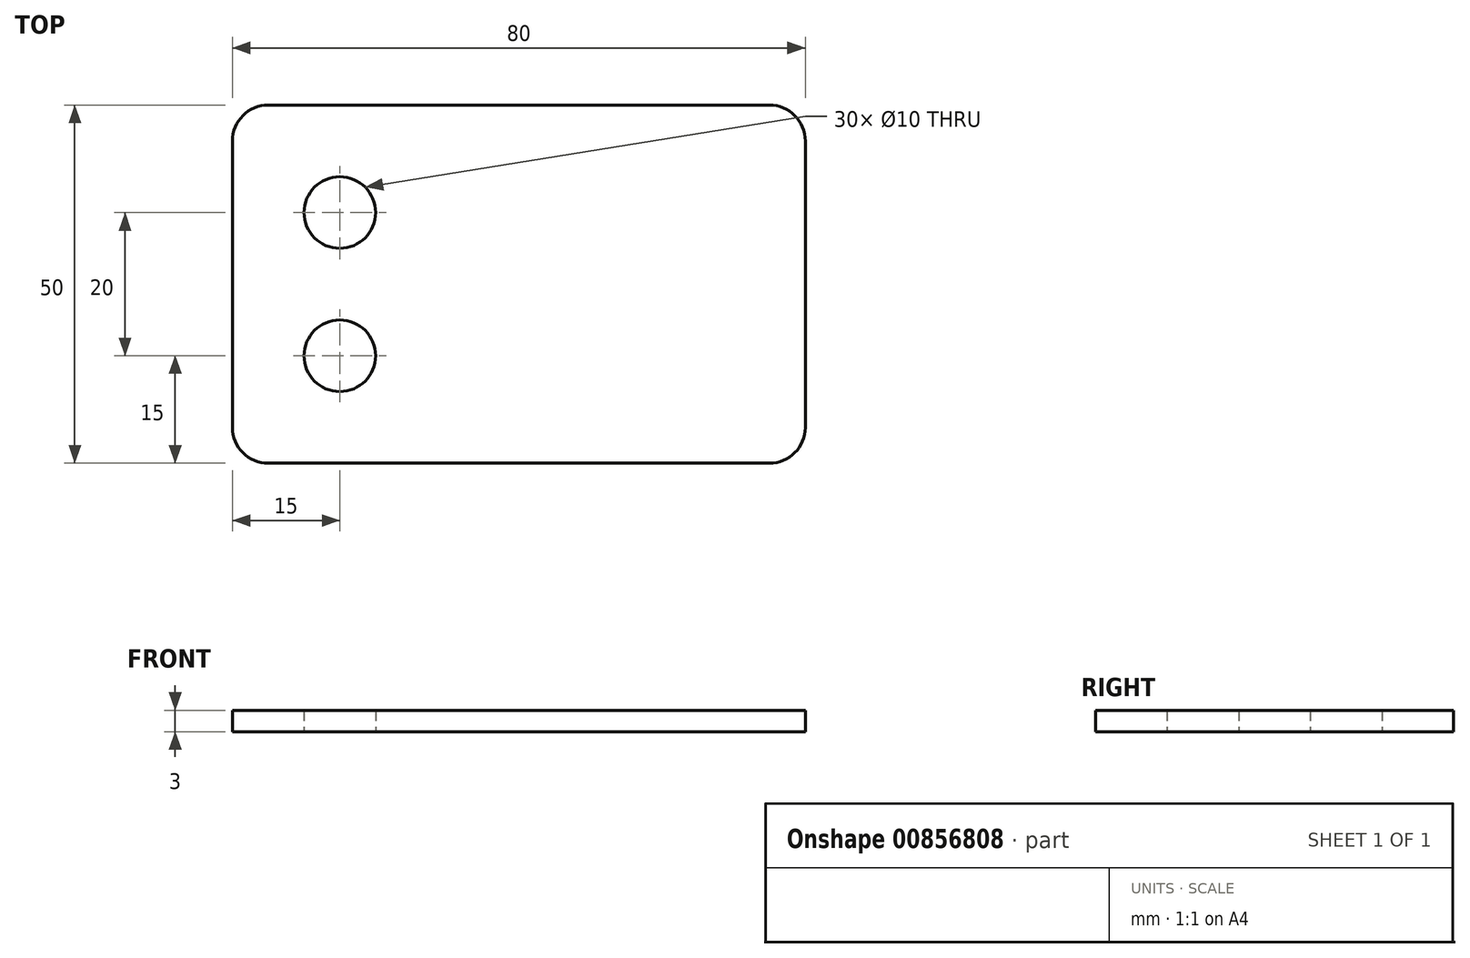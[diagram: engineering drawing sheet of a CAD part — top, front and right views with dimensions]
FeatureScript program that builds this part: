
annotation { "Feature Type Name" : "Feature", "Feature Type Description" : "" }
export const myFeature = defineFeature(function(context is Context, id is Id, definition is map)
    precondition{}
    {
        {
            var Q0;
            Q0=qCreatedBy(makeId("Top.planeOp"),FACE);
            var sketch = newSketch(context, id + "F0", { "sketchPlane" : qUnion([Q0])});
            skLineSegment(sketch, "E0.bottom", {"start": v(40, 25) * mm, "end": v(-40, 25) * mm});
            skLineSegment(sketch, "E0.top", {"start": v(40, -25) * mm, "end": v(-40, -25) * mm});
            skLineSegment(sketch, "E0.left", {"start": v(40, 25) * mm, "end": v(40, -25) * mm});
            skLineSegment(sketch, "E0.right", {"start": v(-40, 25) * mm, "end": v(-40, -25) * mm});
            skPoint(sketch, "E0.middle", {"position": v(0, 0) * mm});
            skCircle(sketch, "E1", {"center": v(-25, 10) * mm, "radius": 5 * mm});
            skCircle(sketch, "E2", {"center": v(-25, -10) * mm, "radius": 5 * mm});
            skSolve(sketch);
        }
        {
            var Q0;
            Q0=makeQuery(id+"F0.imprint","IMPRINT",FACE,{"disambiguationData":[TD([[makeQuery(id+"F0.imprint","IMPRINT",EDGE,{"derivedFrom":sQuery(id+"F0.wireOp",EDGE,"E0.bottom")}),1.0]])]});
            extrude(context, id + "F1", {"entities" : qUnion([Q0]), "depth" : 3 * mm, "offsetDistance" : 25 * mm});
        }
        {
            var Q0;
            Q0=makeQuery(id+"F1.opExtrude","SWEPT_EDGE",EDGE,{"disambiguationData":[OSD([sQuery(id+"F0.wireOp",EDGE,"E0.bottom"),sQuery(id+"F0.wireOp",EDGE,"E0.right")])]});
            var Q1;
            Q1=makeQuery(id+"F1.opExtrude","SWEPT_EDGE",EDGE,{"disambiguationData":[OSD([sQuery(id+"F0.wireOp",EDGE,"E0.top"),sQuery(id+"F0.wireOp",EDGE,"E0.right")])]});
            var Q2;
            Q2=makeQuery(id+"F1.opExtrude","SWEPT_EDGE",EDGE,{"disambiguationData":[OSD([sQuery(id+"F0.wireOp",EDGE,"E0.bottom"),sQuery(id+"F0.wireOp",EDGE,"E0.left")])]});
            var Q3;
            Q3=makeQuery(id+"F1.opExtrude","SWEPT_EDGE",EDGE,{"disambiguationData":[OSD([sQuery(id+"F0.wireOp",EDGE,"E0.top"),sQuery(id+"F0.wireOp",EDGE,"E0.left")])]});
            fillet(context, id + "F2", {"entities" : qUnion([Q0, Q1, Q2, Q3]), "radius" : 5 * mm, "tangentPropagation" : true, "allowEdgeOverflow" : false});
        }
    });
